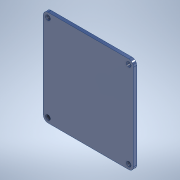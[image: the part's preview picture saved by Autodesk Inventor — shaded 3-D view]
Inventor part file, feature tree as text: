
AUTODESK INVENTOR PART (.ipt)
format: ipt  version: 2020 (Build 240168000, 168)  size: 119,808 bytes
history: native  units: mm
features: other x3, extrude x2, sketch x2, plane x1, reference x1
ambient origin geometry x8: Origin, YZ Plane, XZ Plane, XY Plane, X Axis, Y Axis, Z Axis, Center Point
bodies: 实体1 (feature_tree)
feature tree (9):
  plane  "工作平面1"
  extrude  "拉伸1"  Depth=4.0mm
  extrude  "拉伸2"  Depth=4.0mm
  sketch  "草图1"  dims[d0=4.0mm d1=0.0mm d2=0.5mm]
  reference  "参考1"
  sketch  "草图2"  dims[d3=0.5mm d4=0.5mm d5=0.5mm d6=4.0mm d7=0.0mm]
  other  "<userpath>\Desktop\ME_course_project\课设试试\shaft_try_1.iam"
  other  "shaft_try_1.iam"
  other  "shang(1):1"
